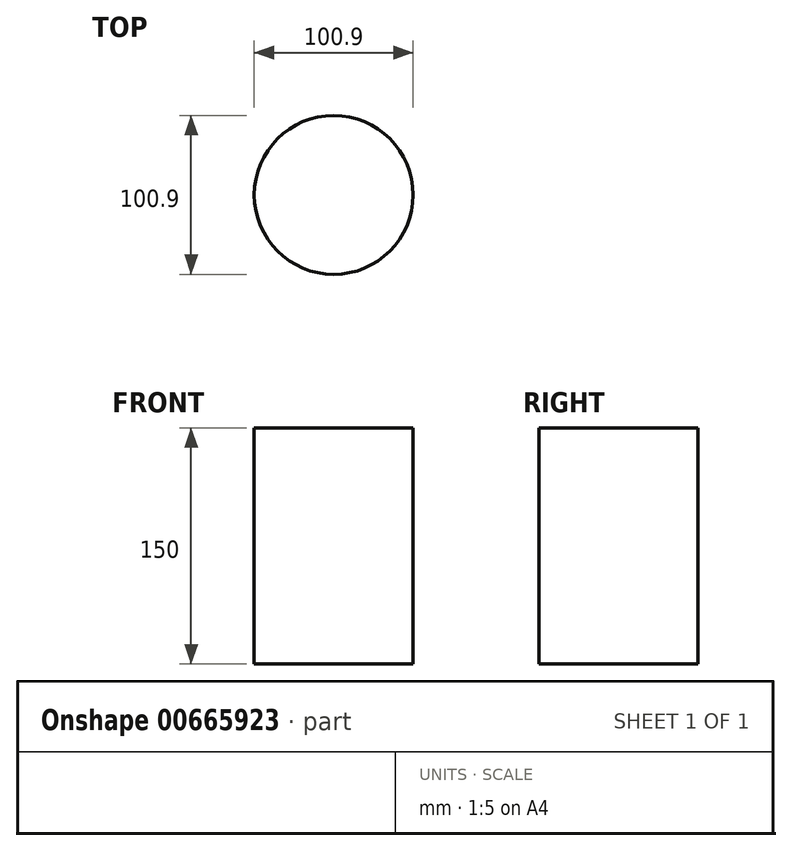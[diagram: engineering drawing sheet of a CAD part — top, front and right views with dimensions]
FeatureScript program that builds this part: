
annotation { "Feature Type Name" : "Feature", "Feature Type Description" : "" }
export const myFeature = defineFeature(function(context is Context, id is Id, definition is map)
    precondition{}
    {
        {
            var Q0;
            Q0=qCreatedBy(makeId("Top.planeOp"),FACE);
            var sketch = newSketch(context, id + "F0", { "sketchPlane" : qUnion([Q0])});
            skCircle(sketch, "E0", {"center": v(0, 0) * mm, "radius": 50.45 * mm});
            skSolve(sketch);
        }
        {
            var Q0;
            Q0 = qSketchRegion(id + "F0", true);
            extrude(context, id + "F1", {"entities" : qUnion([Q0]), "depth" : 150 * mm, "offsetDistance" : 25 * mm});
        }
    });
